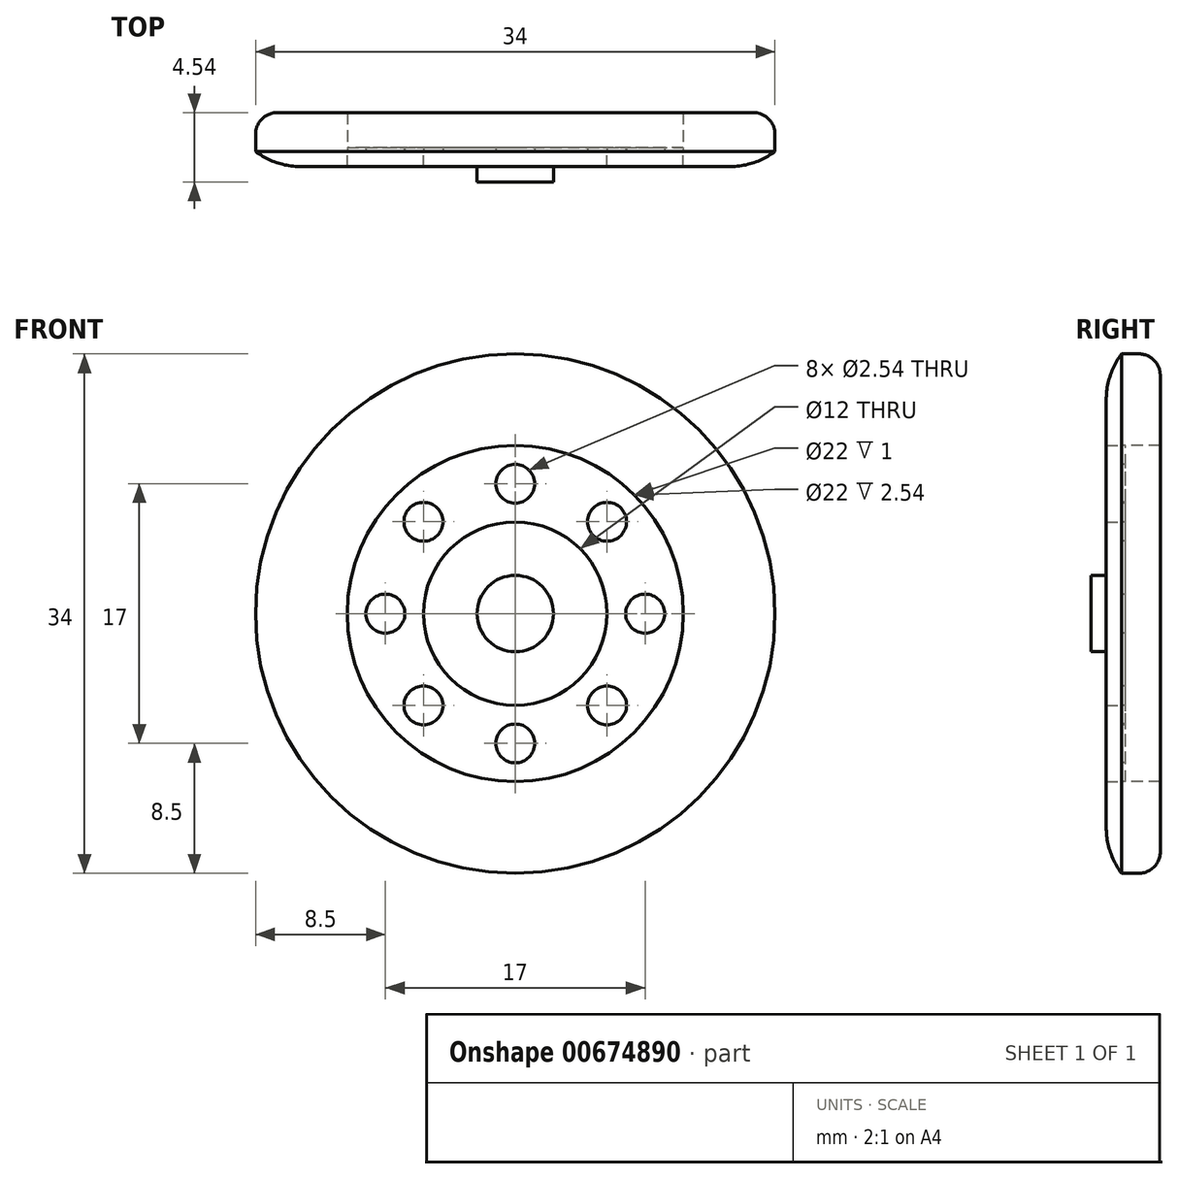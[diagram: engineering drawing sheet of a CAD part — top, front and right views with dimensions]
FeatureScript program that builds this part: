
annotation { "Feature Type Name" : "Feature", "Feature Type Description" : "" }
export const myFeature = defineFeature(function(context is Context, id is Id, definition is map)
    precondition{}
    {
        {
            var Q0;
            Q0=qCreatedBy(makeId("Front.planeOp"),FACE);
            var sketch = newSketch(context, id + "F0", { "sketchPlane" : qUnion([Q0])});
            skCircle(sketch, "E0", {"center": v(0, 0) * mm, "radius": 17 * mm});
            skSolve(sketch);
        }
        {
            var Q0;
            Q0=makeQuery(id+"F0.imprint","IMPRINT",FACE,{"disambiguationData":[TD([[makeQuery(id+"F0.imprint","IMPRINT",EDGE,{"derivedFrom":sQuery(id+"F0.wireOp",EDGE,"E0")}),1.0]])]});
            var sketch = newSketch(context, id + "F1", { "sketchPlane" : qUnion([Q0])});
            skCircle(sketch, "E1", {"center": v(0, 0) * mm, "radius": 11 * mm});
            skCircle(sketch, "E2", {"center": v(0, 0) * mm, "radius": 6 * mm});
            skCircle(sketch, "E3", {"center": v(0, 0) * mm, "radius": 2.5 * mm});
            skLineSegment(sketch, "E4", {"start": v(0, 6) * mm, "end": v(0, 8.5) * mm});
            skCircle(sketch, "E5", {"center": v(0, 8.5) * mm, "radius": 1.27 * mm});
            skCircle(sketch, "E6.1.0", {"center": v(-6.01, 6.01) * mm, "radius": 1.27 * mm});
            skCircle(sketch, "E6.2.0", {"center": v(-8.5, 0) * mm, "radius": 1.27 * mm});
            skCircle(sketch, "E7.1.3.0", {"center": v(-6.01, -6.01) * mm, "radius": 1.27 * mm});
            skCircle(sketch, "E7.1.4.0", {"center": v(0, -8.5) * mm, "radius": 1.27 * mm});
            skCircle(sketch, "E7.1.5.0", {"center": v(6.01, -6.01) * mm, "radius": 1.27 * mm});
            skCircle(sketch, "E7.1.6.0", {"center": v(8.5, 0) * mm, "radius": 1.27 * mm});
            skCircle(sketch, "E7.1.7.0", {"center": v(6.01, 6.01) * mm, "radius": 1.27 * mm});
            skSolve(sketch);
        }
        {
            var Q0;
            Q0=makeQuery(id+"F1.imprint","IMPRINT",FACE,{"disambiguationData":[TD([[makeQuery(id+"F1.imprint","IMPRINT",EDGE,{"derivedFrom":sQuery(id+"F1.wireOp",EDGE,"E1")}),-1.0]])]});
            var Q1;
            Q1=makeQuery(id+"F1.imprint","IMPRINT",FACE,{"disambiguationData":[TD([[makeQuery(id+"F1.imprint","IMPRINT",EDGE,{"derivedFrom":sQuery(id+"F1.wireOp",EDGE,"E2")}),1.0]])]});
            extrude(context, id + "F2", {"entities" : qUnion([Q0, Q1]), "depth" : 1 * mm, "offsetDistance" : 25.4 * mm});
        }
        {
            var Q0;
            Q0=makeQuery(id+"F1.imprint","IMPRINT",FACE,{"disambiguationData":[TD([[makeQuery(id+"F1.imprint","IMPRINT",EDGE,{"derivedFrom":sQuery(id+"F1.wireOp",EDGE,"E3")}),1.0]])]});
            extrude(context, id + "F3", {"entities" : qUnion([Q0]), "operationType" : NewBodyOperationType.ADD, "depth" : 2 * mm, "offsetDistance" : 25.4 * mm});
        }
        {
            var Q0;
            Q0 = qSketchRegion(id + "F1", true);
            extrude(context, id + "F4", {"entities" : qUnion([Q0]), "oppositeDirection" : true, "depth" : 0.25 * mm, "offsetDistance" : 25.4 * mm});
        }
        {
            var Q0;
            Q0=makeQuery(id+"F2.opExtrude","CAP_EDGE",EDGE,{"disambiguationData":[OSD([sQuery(id+"F0.wireOp",EDGE,"E0")])],"isStart":false});
            fillet(context, id + "F5", {"entities" : qUnion([Q0]), "radius" : 5.08 * mm, "tangentPropagation" : true, "allowEdgeOverflow" : false});
        }
        {
            var Q0;
            Q0=makeQuery(id+"F1.imprint","IMPRINT",FACE,{"disambiguationData":[TD([[makeQuery(id+"F1.imprint","IMPRINT",EDGE,{"derivedFrom":sQuery(id+"F1.wireOp",EDGE,"E1")}),-1.0]])]});
            extrude(context, id + "F6", {"entities" : qUnion([Q0]), "oppositeDirection" : true, "depth" : 2.54 * mm, "offsetDistance" : 25.4 * mm});
        }
        {
            var Q0;
            Q0=makeQuery(id+"F6.opExtrude","CAP_EDGE",EDGE,{"disambiguationData":[OSD([sQuery(id+"F0.wireOp",EDGE,"E0")])],"isStart":false});
            fillet(context, id + "F7", {"entities" : qUnion([Q0]), "radius" : 1.41 * mm, "tangentPropagation" : true, "allowEdgeOverflow" : false});
        }
    });
